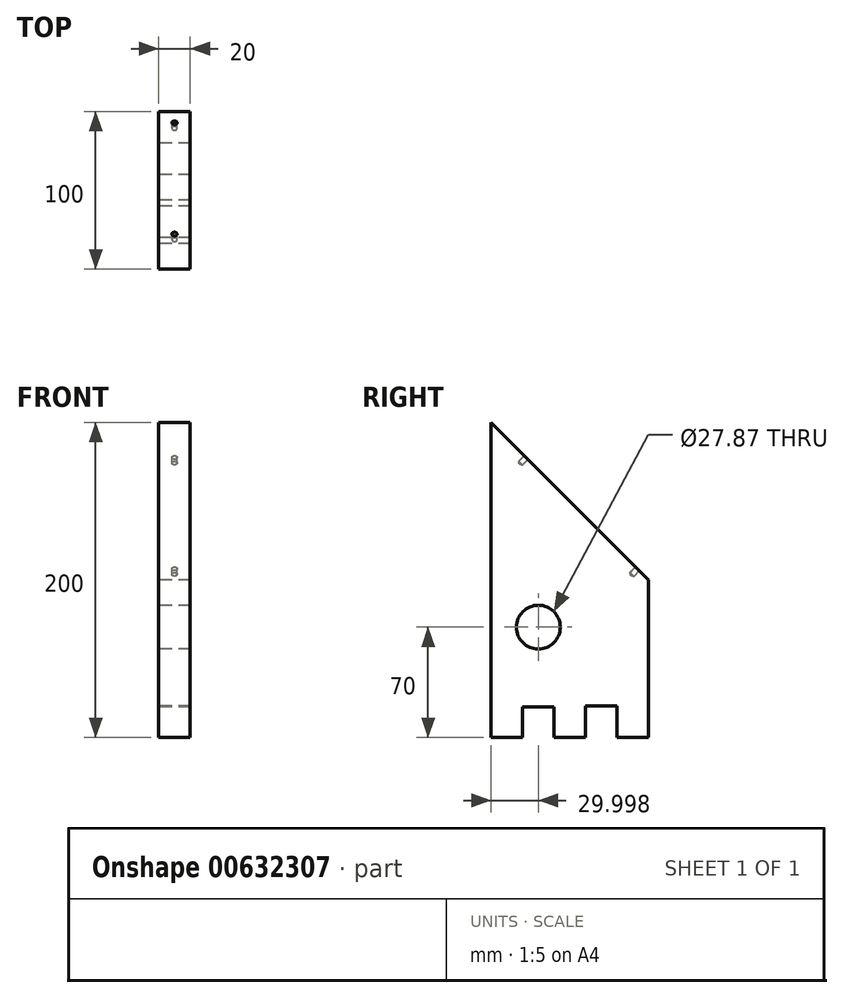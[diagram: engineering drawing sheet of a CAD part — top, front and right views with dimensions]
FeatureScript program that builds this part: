
annotation { "Feature Type Name" : "Feature", "Feature Type Description" : "" }
export const myFeature = defineFeature(function(context is Context, id is Id, definition is map)
    precondition{}
    {
        {
            var Q0;
            Q0=qCreatedBy(makeId("Right.planeOp"),FACE);
            var sketch = newSketch(context, id + "F0", { "sketchPlane" : qUnion([Q0])});
            skLineSegment(sketch, "E0.bottom", {"start": v(-65.31, 0) * mm, "end": v(34.69, 0) * mm});
            skLineSegment(sketch, "E0.top", {"start": v(-65.31, 100) * mm, "end": v(34.69, 100) * mm});
            skLineSegment(sketch, "E0.left", {"start": v(-65.31, 0) * mm, "end": v(-65.31, 100) * mm});
            skLineSegment(sketch, "E0.right", {"start": v(34.69, 0) * mm, "end": v(34.69, 100) * mm});
            skLineSegment(sketch, "E1", {"start": v(-65.31, 100) * mm, "end": v(-65.31, 200) * mm});
            skLineSegment(sketch, "E2", {"start": v(-65.31, 200) * mm, "end": v(34.69, 100) * mm});
            skCircle(sketch, "E3", {"center": v(-35.31, 70) * mm, "radius": 13.93 * mm});
            skLineSegment(sketch, "E4.bottom", {"start": v(-45.31, 0) * mm, "end": v(-25.31, 0) * mm});
            skLineSegment(sketch, "E4.top", {"start": v(-45.31, 19.4) * mm, "end": v(-25.31, 19.4) * mm});
            skLineSegment(sketch, "E4.left", {"start": v(-45.31, 0) * mm, "end": v(-45.31, 19.4) * mm});
            skLineSegment(sketch, "E4.right", {"start": v(-25.31, 0) * mm, "end": v(-25.31, 19.4) * mm});
            skLineSegment(sketch, "E5.bottom", {"start": v(-5.31, 0) * mm, "end": v(14.69, 0) * mm});
            skLineSegment(sketch, "E5.top", {"start": v(-5.31, 20) * mm, "end": v(14.69, 20) * mm});
            skLineSegment(sketch, "E5.left", {"start": v(-5.31, 0) * mm, "end": v(-5.31, 20) * mm});
            skLineSegment(sketch, "E5.right", {"start": v(14.69, 0) * mm, "end": v(14.69, 20) * mm});
            skSolve(sketch);
        }
        {
            var Q0;
            Q0=makeQuery(id+"F0.imprint","IMPRINT",FACE,{"disambiguationData":[TD([[makeQuery(id+"F0.imprint","IMPRINT",EDGE,{"derivedFrom":sQuery(id+"F0.wireOp",EDGE,"E0.top")}),1.0]])]});
            var Q1;
            Q1=makeQuery(id+"F0.imprint","IMPRINT",FACE,{"disambiguationData":[TD([[makeQuery(id+"F0.imprint","IMPRINT",EDGE,{"derivedFrom":sQuery(id+"F0.wireOp",EDGE,"E0.bottom")}),1.0]])]});
            extrude(context, id + "F1", {"entities" : qUnion([Q0, Q1]), "depth" : 20 * mm, "offsetDistance" : 25 * mm});
        }
        {
            var Q0;
            Q0=makeQuery(id+"F1.opExtrude","SWEPT_FACE",FACE,{"disambiguationData":[OSD([sQuery(id+"F0.wireOp",EDGE,"E2")])]});
            var sketch = newSketch(context, id + "F2", { "sketchPlane" : qUnion([Q0])});
            skLineSegment(sketch, "E6", {"start": v(-10, 46.18) * mm, "end": v(-10, 187.6) * mm, "construction": true});
            skPoint(sketch, "E7", {"position": v(-10, 56.18) * mm});
            skPoint(sketch, "E8", {"position": v(-10, 156.18) * mm});
            skSolve(sketch);
        }
        {
            var Q0;
            Q0=sQuery(id+"F2.wireOp",VERTEX,"E7");
            var Q1;
            Q1=sQuery(id+"F2.wireOp",VERTEX,"E8");
            var Q2;
            Q2=makeQuery(id+"F1.opExtrude","SWEPT_BODY",BODY,{"disambiguationData":[OSD([sQuery(id+"F0.wireOp",EDGE,"E0.bottom"),sQuery(id+"F0.wireOp",EDGE,"E0.left"),sQuery(id+"F0.wireOp",EDGE,"E0.right"),sQuery(id+"F0.wireOp",EDGE,"E1"),sQuery(id+"F0.wireOp",EDGE,"E2")])]});
            hole(context, id + "F3", {"style" : HoleStyle.SIMPLE, "endStyle" : HoleEndStyle.BLIND, "standardTappedOrClearance" : lookupTablePath({ "standard" : "ISO", "fit" : "Normal", "size" : "M3", "type" : "Clearance" }), "standardBlindInLast" : lookupTablePath({ "fit" : "Standard", "standard" : "ISO", "size" : "M3", "type" : "Clearance" }), "holeDiameter" : 3.3 * mm, "majorDiameter" : 5 * mm, "holeDepth" : 5 * mm, "isTappedThrough" : true, "tappedDepth" : 12 * mm, "tapClearance" : 3, "locations" : qUnion([Q0, Q1]), "scope" : qUnion([Q2])});
        }
    });
